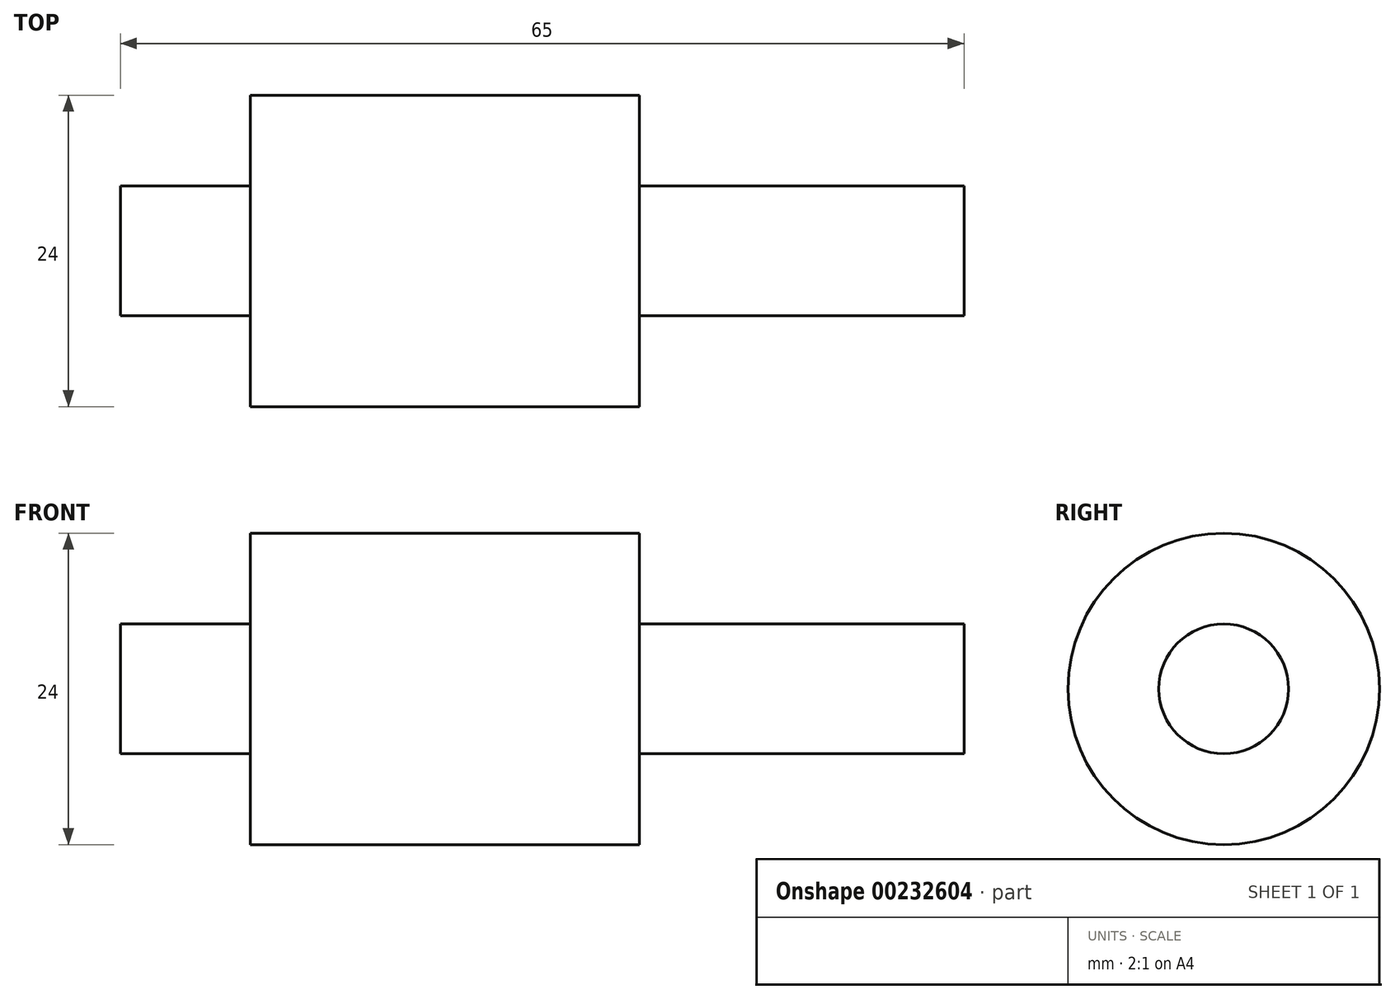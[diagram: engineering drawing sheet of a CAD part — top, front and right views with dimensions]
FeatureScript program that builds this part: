
annotation { "Feature Type Name" : "Feature", "Feature Type Description" : "" }
export const myFeature = defineFeature(function(context is Context, id is Id, definition is map)
    precondition{}
    {
        {
            var Q0;
            Q0=qCreatedBy(makeId("Front.planeOp"),FACE);
            var sketch = newSketch(context, id + "F0", { "sketchPlane" : qUnion([Q0])});
            skLineSegment(sketch, "E0", {"start": v(0, 0) * mm, "end": v(0, 5) * mm});
            skLineSegment(sketch, "E1", {"start": v(0, 5) * mm, "end": v(10, 5) * mm});
            skLineSegment(sketch, "E2", {"start": v(10, 5) * mm, "end": v(10, 12) * mm});
            skLineSegment(sketch, "E3", {"start": v(10, 12) * mm, "end": v(40, 12) * mm});
            skLineSegment(sketch, "E4", {"start": v(40, 12) * mm, "end": v(40, 5) * mm});
            skLineSegment(sketch, "E5", {"start": v(40, 5) * mm, "end": v(65, 5) * mm});
            skLineSegment(sketch, "E6", {"start": v(65, 5) * mm, "end": v(65, 0) * mm});
            skLineSegment(sketch, "E7", {"start": v(65, 0) * mm, "end": v(0, 0) * mm});
            skSolve(sketch);
        }
        {
            var Q0;
            Q0 = qSketchRegion(id + "F0", true);
            var Q1;
            Q1=sQuery(id+"F0.wireOp",EDGE,"E7");
            revolve(context, id + "F1", {"entities" : qUnion([Q0]), "axis" : qUnion([Q1]), "revolveType" : RevolveType.FULL});
        }
    });
